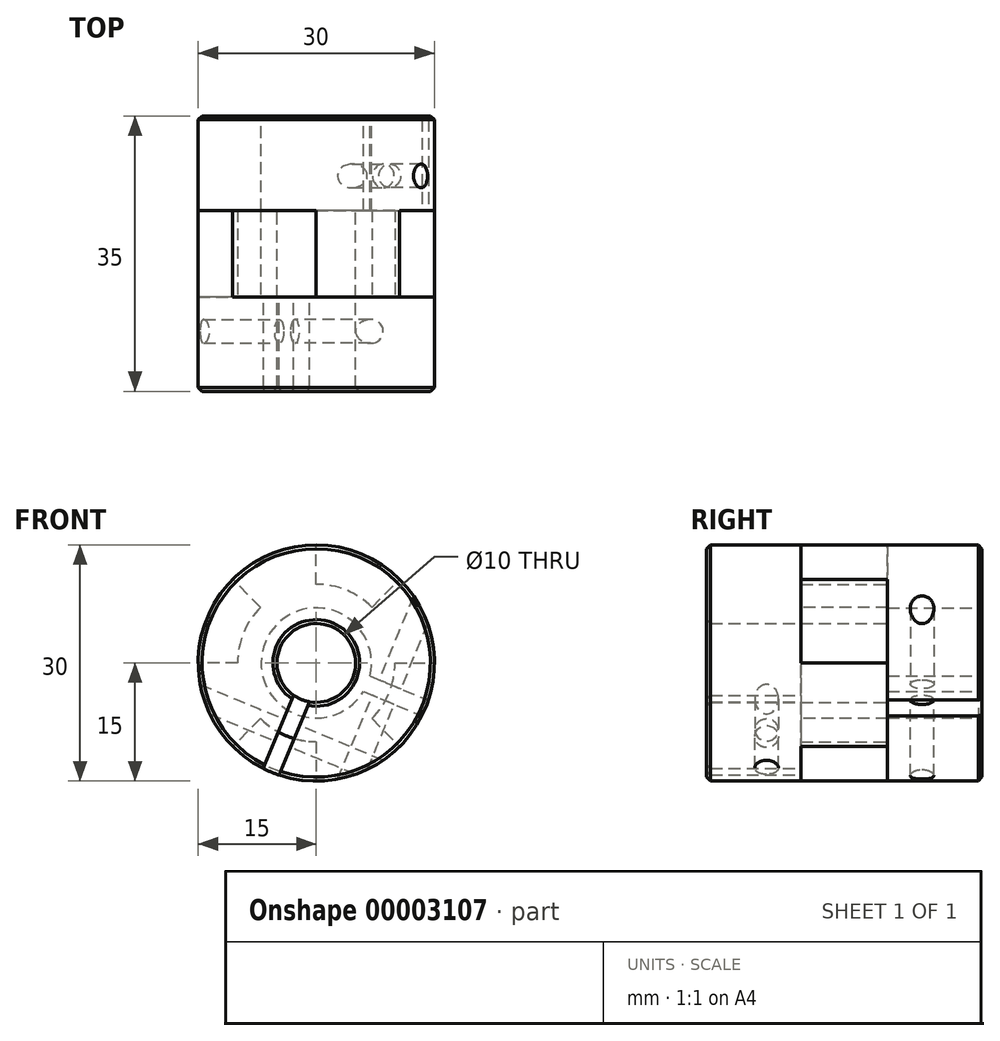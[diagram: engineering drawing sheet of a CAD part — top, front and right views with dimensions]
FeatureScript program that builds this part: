
annotation { "Feature Type Name" : "Feature", "Feature Type Description" : "" }
export const myFeature = defineFeature(function(context is Context, id is Id, definition is map)
    precondition{}
    {
        {
            var Q0;
            Q0=qCreatedBy(makeId("Front.planeOp"),FACE);
            var sketch = newSketch(context, id + "F0", { "sketchPlane" : qUnion([Q0])});
            skCircle(sketch, "E0", {"center": v(0, 0) * mm, "radius": 15 * mm});
            skCircle(sketch, "E1", {"center": v(0, 0) * mm, "radius": 5 * mm});
            skLineSegment(sketch, "E2", {"start": v(0, 5) * mm, "end": v(0, 15) * mm});
            skLineSegment(sketch, "E3", {"start": v(5, 0) * mm, "end": v(15, 0) * mm});
            skLineSegment(sketch, "E4", {"start": v(-5, 0) * mm, "end": v(-15, 0) * mm});
            skLineSegment(sketch, "E5", {"start": v(3.54, 3.54) * mm, "end": v(10.6, 10.6) * mm});
            skLineSegment(sketch, "E6", {"start": v(-10.6, 10.6) * mm, "end": v(-3.54, 3.54) * mm});
            skLineSegment(sketch, "E7", {"start": v(3.54, -3.54) * mm, "end": v(10.6, -10.6) * mm});
            skPoint(sketch, "E8.orphan", {"position": v(0, -15) * mm});
            skLineSegment(sketch, "E9", {"start": v(0, -5) * mm, "end": v(0, -15) * mm});
            skLineSegment(sketch, "E10", {"start": v(-3.54, -3.54) * mm, "end": v(-10.6, -10.6) * mm});
            skLineSegment(sketch, "E11", {"start": v(0, 0) * mm, "end": v(13.86, -5.74) * mm, "construction": true});
            skLineSegment(sketch, "E12", {"start": v(4.92, -0.87) * mm, "end": v(14.24, -4.73) * mm});
            skLineSegment(sketch, "E13", {"start": v(4.1, -2.87) * mm, "end": v(13.4, -6.73) * mm});
            skCircle(sketch, "E14", {"center": v(0, 0) * mm, "radius": 10 * mm});
            skSolve(sketch);
        }
        {
            var Q0;
            {var subQ1=sQuery(id+"F0.wireOp",EDGE,"E2");Q0=makeQuery(id+"F0.imprint","IMPRINT",FACE,{"disambiguationData":[TD([[makeQuery(id+"F0.imprint","IMPRINT",EDGE,{"derivedFrom":subQ1}),1.0]])]});}
            var Q1;
            {var subQ1=sQuery(id+"F0.wireOp",EDGE,"E9");Q1=makeQuery(id+"F0.imprint","IMPRINT",FACE,{"disambiguationData":[TD([[makeQuery(id+"F0.imprint","IMPRINT",EDGE,{"derivedFrom":subQ1}),-1.0]])]});}
            var Q2;
            {var subQ1=sQuery(id+"F0.wireOp",EDGE,"E5");Q2=makeQuery(id+"F0.imprint","IMPRINT",FACE,{"disambiguationData":[TD([[makeQuery(id+"F0.imprint","IMPRINT",EDGE,{"derivedFrom":subQ1}),-1.0]])]});}
            var Q3;
            {var subQ1=sQuery(id+"F0.wireOp",EDGE,"E2");Q3=makeQuery(id+"F0.imprint","IMPRINT",FACE,{"disambiguationData":[TD([[makeQuery(id+"F0.imprint","IMPRINT",EDGE,{"derivedFrom":subQ1}),-1.0]])]});}
            var Q4;
            {var subQ1=sQuery(id+"F0.wireOp",EDGE,"E9");Q4=makeQuery(id+"F0.imprint","IMPRINT",FACE,{"disambiguationData":[TD([[makeQuery(id+"F0.imprint","IMPRINT",EDGE,{"derivedFrom":subQ1}),1.0]])]});}
            var Q5;
            {var subQ1=sQuery(id+"F0.wireOp",EDGE,"E4");Q5=makeQuery(id+"F0.imprint","IMPRINT",FACE,{"disambiguationData":[TD([[makeQuery(id+"F0.imprint","IMPRINT",EDGE,{"derivedFrom":subQ1}),-1.0]])]});}
            var Q6;
            {var subQ1=sQuery(id+"F0.wireOp",EDGE,"E4");Q6=makeQuery(id+"F0.imprint","IMPRINT",FACE,{"disambiguationData":[TD([[makeQuery(id+"F0.imprint","IMPRINT",EDGE,{"derivedFrom":subQ1}),1.0]])]});}
            var Q7;
            {var subQ0=sQuery(id+"F0.wireOp",EDGE,"E7");Q7=makeQuery(id+"F0.imprint","IMPRINT",FACE,{"disambiguationData":[TD([[makeQuery(id+"F0.imprint","IMPRINT",EDGE,{"derivedFrom":subQ0}),1.0]])]});}
            var Q8;
            {var subQ1=sQuery(id+"F0.wireOp",EDGE,"E3");Q8=makeQuery(id+"F0.imprint","IMPRINT",FACE,{"disambiguationData":[TD([[makeQuery(id+"F0.imprint","IMPRINT",EDGE,{"derivedFrom":subQ1}),-1.0]])]});}
            extrude(context, id + "F1", {"entities" : qUnion([Q0, Q1, Q2, Q3, Q4, Q5, Q6, Q7, Q8]), "oppositeDirection" : true, "depth" : 12 * mm});
        }
        {
            var Q0;
            {var subQ3=sQuery(id+"F0.wireOp",EDGE,"E9");var subQ5=sQuery(id+"F0.wireOp",EDGE,"E0");var subQ7=makeQuery(id+"F0.imprint","INTERSECT",VERTEX,{"derivedFrom":[subQ5,subQ3]});Q0=makeQuery(id+"F0.imprint","IMPRINT",FACE,{"disambiguationData":[TD([[makeQuery(id+"F0.imprint","IMPRINT",EDGE,{"disambiguationData":[TD([[subQ7,1.0]])],"derivedFrom":subQ5}),1.0]])]});}
            var Q1;
            {var subQ3=sQuery(id+"F0.wireOp",EDGE,"E2");var subQ5=sQuery(id+"F0.wireOp",EDGE,"E0");var subQ7=makeQuery(id+"F0.imprint","INTERSECT",VERTEX,{"derivedFrom":[subQ5,subQ3]});Q1=makeQuery(id+"F0.imprint","IMPRINT",FACE,{"disambiguationData":[TD([[makeQuery(id+"F0.imprint","IMPRINT",EDGE,{"disambiguationData":[TD([[subQ7,1.0]])],"derivedFrom":subQ5}),1.0]])]});}
            extrude(context, id + "F2", {"entities" : qUnion([Q0, Q1]), "operationType" : NewBodyOperationType.ADD, "depth" : 11 * mm});
        }
        {
            var Q0;
            {var subQ3=sQuery(id+"F0.wireOp",EDGE,"E2");var subQ5=sQuery(id+"F0.wireOp",EDGE,"E0");var subQ7=makeQuery(id+"F0.imprint","INTERSECT",VERTEX,{"derivedFrom":[subQ5,subQ3]});Q0=makeQuery(id+"F0.imprint","IMPRINT",FACE,{"disambiguationData":[TD([[makeQuery(id+"F0.imprint","IMPRINT",EDGE,{"disambiguationData":[TD([[subQ7,-1.0]])],"derivedFrom":subQ5}),1.0]])]});}
            var Q1;
            {var subQ3=sQuery(id+"F0.wireOp",EDGE,"E7");var subQ5=sQuery(id+"F0.wireOp",EDGE,"E0");var subQ7=makeQuery(id+"F0.imprint","INTERSECT",VERTEX,{"derivedFrom":[subQ5,subQ3]});Q1=makeQuery(id+"F0.imprint","IMPRINT",FACE,{"disambiguationData":[TD([[makeQuery(id+"F0.imprint","IMPRINT",EDGE,{"disambiguationData":[TD([[subQ7,1.0]])],"derivedFrom":subQ5}),1.0]])]});}
            var Q2;
            {var subQ3=sQuery(id+"F0.wireOp",EDGE,"E3");var subQ5=sQuery(id+"F0.wireOp",EDGE,"E0");var subQ7=makeQuery(id+"F0.imprint","INTERSECT",VERTEX,{"derivedFrom":[subQ5,subQ3]});Q2=makeQuery(id+"F0.imprint","IMPRINT",FACE,{"disambiguationData":[TD([[makeQuery(id+"F0.imprint","IMPRINT",EDGE,{"disambiguationData":[TD([[subQ7,-1.0]])],"derivedFrom":subQ5}),1.0]])]});}
            var Q3;
            {var subQ3=sQuery(id+"F0.wireOp",EDGE,"E4");var subQ5=sQuery(id+"F0.wireOp",EDGE,"E0");var subQ7=makeQuery(id+"F0.imprint","INTERSECT",VERTEX,{"derivedFrom":[subQ5,subQ3]});Q3=makeQuery(id+"F0.imprint","IMPRINT",FACE,{"disambiguationData":[TD([[makeQuery(id+"F0.imprint","IMPRINT",EDGE,{"disambiguationData":[TD([[subQ7,-1.0]])],"derivedFrom":subQ5}),1.0]])]});}
            var Q4;
            {var subQ3=sQuery(id+"F0.wireOp",EDGE,"E1");var subQ5=sQuery(id+"F0.wireOp",EDGE,"E2");var subQ7=makeQuery(id+"F0.imprint","INTERSECT",VERTEX,{"derivedFrom":[subQ3,subQ5]});Q4=makeQuery(id+"F0.imprint","IMPRINT",FACE,{"disambiguationData":[TD([[makeQuery(id+"F0.imprint","IMPRINT",EDGE,{"disambiguationData":[TD([[subQ7,-1.0]])],"derivedFrom":subQ3}),-1.0]])]});}
            var Q5;
            {var subQ3=sQuery(id+"F0.wireOp",EDGE,"E4");var subQ5=sQuery(id+"F0.wireOp",EDGE,"E1");var subQ7=makeQuery(id+"F0.imprint","INTERSECT",VERTEX,{"derivedFrom":[subQ5,subQ3]});Q5=makeQuery(id+"F0.imprint","IMPRINT",FACE,{"disambiguationData":[TD([[makeQuery(id+"F0.imprint","IMPRINT",EDGE,{"disambiguationData":[TD([[subQ7,-1.0]])],"derivedFrom":subQ5}),-1.0]])]});}
            var Q6;
            {var subQ3=sQuery(id+"F0.wireOp",EDGE,"E7");var subQ5=sQuery(id+"F0.wireOp",EDGE,"E1");var subQ7=makeQuery(id+"F0.imprint","INTERSECT",VERTEX,{"derivedFrom":[subQ5,subQ3]});Q6=makeQuery(id+"F0.imprint","IMPRINT",FACE,{"disambiguationData":[TD([[makeQuery(id+"F0.imprint","IMPRINT",EDGE,{"disambiguationData":[TD([[subQ7,1.0]])],"derivedFrom":subQ5}),-1.0]])]});}
            var Q7;
            {var subQ3=sQuery(id+"F0.wireOp",EDGE,"E3");var subQ5=sQuery(id+"F0.wireOp",EDGE,"E1");var subQ7=makeQuery(id+"F0.imprint","INTERSECT",VERTEX,{"derivedFrom":[subQ5,subQ3]});Q7=makeQuery(id+"F0.imprint","IMPRINT",FACE,{"disambiguationData":[TD([[makeQuery(id+"F0.imprint","IMPRINT",EDGE,{"disambiguationData":[TD([[subQ7,-1.0]])],"derivedFrom":subQ5}),-1.0]])]});}
            var Q8;
            {var subQ3=sQuery(id+"F0.wireOp",EDGE,"E4");var subQ5=sQuery(id+"F0.wireOp",EDGE,"E1");var subQ7=makeQuery(id+"F0.imprint","INTERSECT",VERTEX,{"derivedFrom":[subQ5,subQ3]});Q8=makeQuery(id+"F0.imprint","IMPRINT",FACE,{"disambiguationData":[TD([[makeQuery(id+"F0.imprint","IMPRINT",EDGE,{"disambiguationData":[TD([[subQ7,1.0]])],"derivedFrom":subQ5}),-1.0]])]});}
            var Q9;
            {var subQ3=sQuery(id+"F0.wireOp",EDGE,"E9");var subQ5=sQuery(id+"F0.wireOp",EDGE,"E1");var subQ7=makeQuery(id+"F0.imprint","INTERSECT",VERTEX,{"derivedFrom":[subQ5,subQ3]});Q9=makeQuery(id+"F0.imprint","IMPRINT",FACE,{"disambiguationData":[TD([[makeQuery(id+"F0.imprint","IMPRINT",EDGE,{"disambiguationData":[TD([[subQ7,1.0]])],"derivedFrom":subQ5}),-1.0]])]});}
            var Q10;
            {var subQ3=sQuery(id+"F0.wireOp",EDGE,"E7");var subQ5=sQuery(id+"F0.wireOp",EDGE,"E1");var subQ7=makeQuery(id+"F0.imprint","INTERSECT",VERTEX,{"derivedFrom":[subQ5,subQ3]});Q10=makeQuery(id+"F0.imprint","IMPRINT",FACE,{"disambiguationData":[TD([[makeQuery(id+"F0.imprint","IMPRINT",EDGE,{"disambiguationData":[TD([[subQ7,-1.0]])],"derivedFrom":subQ5}),-1.0]])]});}
            var Q11;
            {var subQ3=sQuery(id+"F0.wireOp",EDGE,"E3");var subQ5=sQuery(id+"F0.wireOp",EDGE,"E1");var subQ7=makeQuery(id+"F0.imprint","INTERSECT",VERTEX,{"derivedFrom":[subQ5,subQ3]});Q11=makeQuery(id+"F0.imprint","IMPRINT",FACE,{"disambiguationData":[TD([[makeQuery(id+"F0.imprint","IMPRINT",EDGE,{"disambiguationData":[TD([[subQ7,1.0]])],"derivedFrom":subQ5}),-1.0]])]});}
            var Q12;
            {var subQ3=sQuery(id+"F0.wireOp",EDGE,"E2");var subQ5=sQuery(id+"F0.wireOp",EDGE,"E1");var subQ7=makeQuery(id+"F0.imprint","INTERSECT",VERTEX,{"derivedFrom":[subQ5,subQ3]});Q12=makeQuery(id+"F0.imprint","IMPRINT",FACE,{"disambiguationData":[TD([[makeQuery(id+"F0.imprint","IMPRINT",EDGE,{"disambiguationData":[TD([[subQ7,1.0]])],"derivedFrom":subQ5}),-1.0]])]});}
            var Q13;
            {var subQ3=sQuery(id+"F0.wireOp",EDGE,"E12");var subQ5=sQuery(id+"F0.wireOp",EDGE,"E1");var subQ7=makeQuery(id+"F0.imprint","INTERSECT",VERTEX,{"derivedFrom":[subQ5,subQ3]});Q13=makeQuery(id+"F0.imprint","IMPRINT",FACE,{"disambiguationData":[TD([[makeQuery(id+"F0.imprint","IMPRINT",EDGE,{"disambiguationData":[TD([[subQ7,1.0]])],"derivedFrom":subQ5}),-1.0]])]});}
            extrude(context, id + "F3", {"entities" : qUnion([Q0, Q1, Q2, Q3, Q4, Q5, Q6, Q7, Q8, Q9, Q10, Q11, Q12, Q13]), "depth" : 11 * mm});
        }
        {
            var Q0;
            Q0=makeQuery(id+"F1.opExtrude","SWEPT_FACE",FACE,{"disambiguationData":[OSD([sQuery(id+"F0.wireOp",EDGE,"E12")])]});
            var sketch = newSketch(context, id + "F4", { "sketchPlane" : qUnion([Q0])});
            skPoint(sketch, "E15", {"position": v(9.66, -4.38) * mm});
            skSolve(sketch);
        }
        {
            var Q0;
            Q0=sQuery(id+"F4.wireOp",VERTEX,"E15");
            var Q1;
            Q1=makeQuery(id+"F1.opExtrude","SWEPT_BODY",BODY,{"disambiguationData":[OSD([sQuery(id+"F0.wireOp",EDGE,"E0"),sQuery(id+"F0.wireOp",EDGE,"E1"),sQuery(id+"F0.wireOp",EDGE,"E12"),sQuery(id+"F0.wireOp",EDGE,"E13")])]});
            hole(context, id + "F5", {"style" : HoleStyle.SIMPLE, "holeDiameter" : 3 * mm, "endStyle" : HoleEndStyle.THROUGH, "locations" : qUnion([Q0]), "scope" : qUnion([Q1])});
        }
        {
            var Q0;
            Q0=makeQuery(id+"F1.opExtrude","SWEPT_FACE",FACE,{"disambiguationData":[OSD([sQuery(id+"F0.wireOp",EDGE,"E13")])]});
            var sketch = newSketch(context, id + "F6", { "sketchPlane" : qUnion([Q0])});
            skPoint(sketch, "E16", {"position": v(9.66, 4.38) * mm});
            skSolve(sketch);
        }
        {
            var Q0;
            Q0=sQuery(id+"F6.wireOp",VERTEX,"E16");
            var Q1;
            Q1=makeQuery(id+"F1.opExtrude","SWEPT_BODY",BODY,{"disambiguationData":[OSD([sQuery(id+"F0.wireOp",EDGE,"E0"),sQuery(id+"F0.wireOp",EDGE,"E1"),sQuery(id+"F0.wireOp",EDGE,"E12"),sQuery(id+"F0.wireOp",EDGE,"E13")])]});
            hole(context, id + "F7", {"style" : HoleStyle.SIMPLE, "holeDiameter" : 3 * mm, "endStyle" : HoleEndStyle.THROUGH, "locations" : qUnion([Q0]), "scope" : qUnion([Q1])});
        }
        {
            var Q0;
            Q0=makeQuery(id+"F1.opExtrude","SWEPT_BODY",BODY,{"disambiguationData":[OSD([sQuery(id+"F0.wireOp",EDGE,"E0"),sQuery(id+"F0.wireOp",EDGE,"E1"),sQuery(id+"F0.wireOp",EDGE,"E12"),sQuery(id+"F0.wireOp",EDGE,"E13")])]});
            transform(context, id + "F8", {"entities" : qUnion([Q0]), "transformType" : TransformType.TRANSLATION_3D, "dx" : 0 * mm, "dy" : 11 * mm, "dz" : 0 * mm, "makeCopy" : true});
        }
        {
            var Q0;
            Q0=qCreatedBy(makeId("Right.planeOp"),FACE);
            var sketch = newSketch(context, id + "F9", { "sketchPlane" : qUnion([Q0])});
            skLineSegment(sketch, "E17", {"start": v(0, 0) * mm, "end": v(-51.13, 0) * mm});
            skSolve(sketch);
        }
        {
            var Q0;
            Q0=makeQuery(id+"F8.opPattern","COPY",BODY,{"derivedFrom":makeQuery(id+"F1.opExtrude","SWEPT_BODY",BODY,{"disambiguationData":[OSD([sQuery(id+"F0.wireOp",EDGE,"E0"),sQuery(id+"F0.wireOp",EDGE,"E1"),sQuery(id+"F0.wireOp",EDGE,"E12"),sQuery(id+"F0.wireOp",EDGE,"E13")])]}),"instanceName":"1"});
            var Q1;
            Q1=sQuery(id+"F9.wireOp",EDGE,"E17");
            transform(context, id + "F10", {"entities" : qUnion([Q0]), "transformType" : TransformType.ROTATION, "transformAxis" : qUnion([Q1]), "angle" : 90 * degree, "makeCopy" : false});
        }
        {
            var Q0;
            Q0=qCreatedBy(makeId("Front.planeOp"),FACE);
            var sketch = newSketch(context, id + "F11", { "sketchPlane" : qUnion([Q0])});
            skLineSegment(sketch, "E18", {"start": v(-17.32, 7.17) * mm, "end": v(0, 0) * mm});
            skSolve(sketch);
        }
        {
            var Q0;
            Q0=makeQuery(id+"F8.opPattern","COPY",BODY,{"derivedFrom":makeQuery(id+"F1.opExtrude","SWEPT_BODY",BODY,{"disambiguationData":[OSD([sQuery(id+"F0.wireOp",EDGE,"E0"),sQuery(id+"F0.wireOp",EDGE,"E1"),sQuery(id+"F0.wireOp",EDGE,"E12"),sQuery(id+"F0.wireOp",EDGE,"E13")])]}),"instanceName":"1"});
            var Q1;
            Q1=sQuery(id+"F11.wireOp",EDGE,"E18");
            transform(context, id + "F12", {"entities" : qUnion([Q0]), "transformType" : TransformType.ROTATION, "transformAxis" : qUnion([Q1]), "angle" : 180 * degree, "makeCopy" : false});
        }
        {
            var Q0;
            Q0=makeQuery(id+"F1.opExtrude","CAP_FACE",FACE,{"disambiguationData":[OSD([sQuery(id+"F0.wireOp",EDGE,"E0"),sQuery(id+"F0.wireOp",EDGE,"E1"),sQuery(id+"F0.wireOp",EDGE,"E12"),sQuery(id+"F0.wireOp",EDGE,"E13")])],"isStart":false});
            var sketch = newSketch(context, id + "F13", { "sketchPlane" : qUnion([Q0])});
            skCircle(sketch, "E19", {"center": v(0, 0) * mm, "radius": 7 * mm});
            skSolve(sketch);
        }
        {
            var Q0;
            {var subQ3=makeQuery(id+"F1.opExtrude","CAP_EDGE",EDGE,{"disambiguationData":[OSD([sQuery(id+"F0.wireOp",EDGE,"E1")])],"isStart":false});Q0=makeQuery(id+"F13.imprint","IMPRINT",FACE,{"disambiguationData":[TD([[makeQuery(id+"F13.imprint","IMPRINT",EDGE,{"derivedFrom":subQ3}),1.0]])]});}
            extrude(context, id + "F14", {"entities" : qUnion([Q0]), "operationType" : NewBodyOperationType.REMOVE, "oppositeDirection" : true, "depth" : 12 * mm});
        }
        {
            var Q0;
            Q0=makeQuery(id+"F8.opPattern","COPY",EDGE,{"derivedFrom":makeQuery(id+"F1.opExtrude","CAP_EDGE",EDGE,{"disambiguationData":[OSD([sQuery(id+"F0.wireOp",EDGE,"E0")])],"isStart":false}),"instanceName":"1"});
            var Q1;
            Q1=makeQuery(id+"F1.opExtrude","CAP_EDGE",EDGE,{"disambiguationData":[OSD([sQuery(id+"F0.wireOp",EDGE,"E0")])],"isStart":false});
            var Q2;
            Q2=makeQuery(id+"F8.opPattern","COPY",EDGE,{"derivedFrom":makeQuery(id+"F1.opExtrude","CAP_EDGE",EDGE,{"disambiguationData":[OSD([sQuery(id+"F0.wireOp",EDGE,"E1")])],"isStart":false}),"instanceName":"1"});
            var Q3;
            Q3=makeQuery(id+"F14.boolean.opBoolean","COPY",EDGE,{"derivedFrom":makeQuery(id+"F14.opExtrude","CAP_EDGE",EDGE,{"disambiguationData":[OSD([sQuery(id+"F13.wireOp",EDGE,"E19")])],"isStart":true})});
            chamfer(context, id + "F15", {"entities" : qUnion([Q0, Q1, Q2, Q3]), "width" : .5 * mm, "tangentPropagation" : true});
        }
    });
